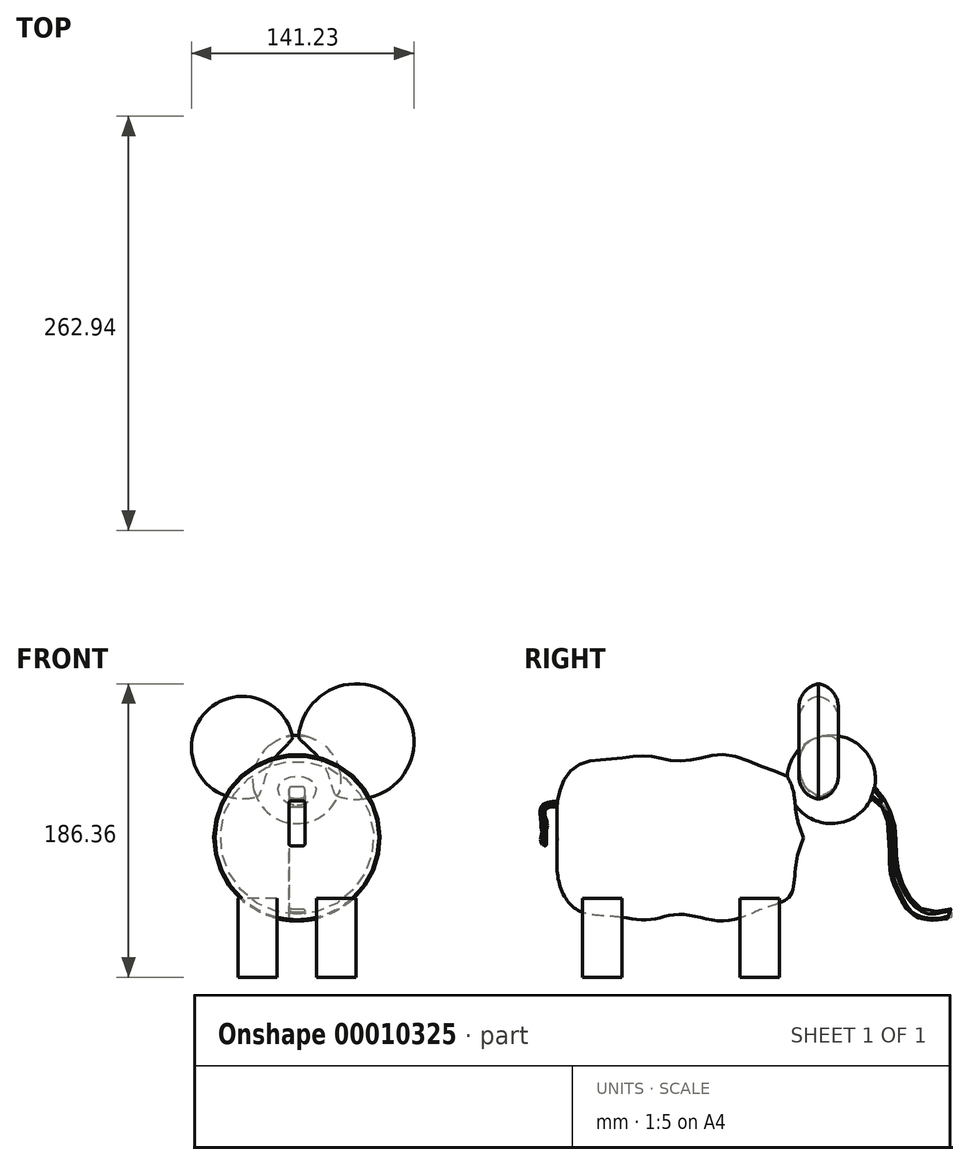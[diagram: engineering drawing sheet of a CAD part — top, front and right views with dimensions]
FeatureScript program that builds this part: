
annotation { "Feature Type Name" : "Feature", "Feature Type Description" : "" }
export const myFeature = defineFeature(function(context is Context, id is Id, definition is map)
    precondition{}
    {
        {
            var Q0;
            Q0=qCreatedBy(makeId("Top.planeOp"),FACE);
            var sketch = newSketch(context, id + "F0", { "sketchPlane" : qUnion([Q0])});
            skLineSegment(sketch, "E0.rect.bottom", {"start": v(25, 50) * mm, "end": v(-25, 50) * mm});
            skLineSegment(sketch, "E0.rect.top", {"start": v(25, -50) * mm, "end": v(-25, -50) * mm});
            skLineSegment(sketch, "E0.rect.left", {"start": v(25, 50) * mm, "end": v(25, -50) * mm});
            skLineSegment(sketch, "E0.rect.right", {"start": v(-25, 50) * mm, "end": v(-25, -50) * mm});
            skPoint(sketch, "E0.rect.middle", {"position": v(0, 0) * mm});
            skCircle(sketch, "E1", {"center": v(-25, 50) * mm, "radius": 12.5 * mm});
            skCircle(sketch, "E2", {"center": v(-25, -50) * mm, "radius": 12.5 * mm});
            skCircle(sketch, "E3", {"center": v(25, -50) * mm, "radius": 12.5 * mm});
            skCircle(sketch, "E4", {"center": v(25, 50) * mm, "radius": 12.5 * mm});
            skSolve(sketch);
        }
        {
            var Q0;
            {var subQ1=sQuery(id+"F0.wireOp",EDGE,"E0.rect.right");var subQ3=sQuery(id+"F0.wireOp",EDGE,"E0.rect.bottom");var subQ5=makeQuery(id+"F0.imprint","INTERSECT",VERTEX,{"derivedFrom":[subQ3,subQ1]});Q0=makeQuery(id+"F0.imprint","IMPRINT",FACE,{"disambiguationData":[TD([[makeQuery(id+"F0.imprint","IMPRINT",EDGE,{"disambiguationData":[TD([[subQ5,1.0]])],"derivedFrom":subQ3}),-1.0]])]});}
            var Q1;
            {var subQ1=sQuery(id+"F0.wireOp",EDGE,"E0.rect.right");var subQ3=sQuery(id+"F0.wireOp",EDGE,"E0.rect.top");var subQ5=makeQuery(id+"F0.imprint","INTERSECT",VERTEX,{"derivedFrom":[subQ3,subQ1]});Q1=makeQuery(id+"F0.imprint","IMPRINT",FACE,{"disambiguationData":[TD([[makeQuery(id+"F0.imprint","IMPRINT",EDGE,{"disambiguationData":[TD([[subQ5,1.0]])],"derivedFrom":subQ3}),1.0]])]});}
            var Q2;
            {var subQ1=sQuery(id+"F0.wireOp",EDGE,"E0.rect.left");var subQ3=sQuery(id+"F0.wireOp",EDGE,"E0.rect.top");var subQ5=makeQuery(id+"F0.imprint","INTERSECT",VERTEX,{"derivedFrom":[subQ3,subQ1]});Q2=makeQuery(id+"F0.imprint","IMPRINT",FACE,{"disambiguationData":[TD([[makeQuery(id+"F0.imprint","IMPRINT",EDGE,{"disambiguationData":[TD([[subQ5,-1.0]])],"derivedFrom":subQ3}),1.0]])]});}
            var Q3;
            {var subQ1=sQuery(id+"F0.wireOp",EDGE,"E0.rect.left");var subQ3=sQuery(id+"F0.wireOp",EDGE,"E0.rect.bottom");var subQ5=makeQuery(id+"F0.imprint","INTERSECT",VERTEX,{"derivedFrom":[subQ3,subQ1]});Q3=makeQuery(id+"F0.imprint","IMPRINT",FACE,{"disambiguationData":[TD([[makeQuery(id+"F0.imprint","IMPRINT",EDGE,{"disambiguationData":[TD([[subQ5,-1.0]])],"derivedFrom":subQ3}),-1.0]])]});}
            var Q4;
            {var subQ1=sQuery(id+"F0.wireOp",EDGE,"E0.rect.right");var subQ3=sQuery(id+"F0.wireOp",EDGE,"E0.rect.bottom");var subQ5=makeQuery(id+"F0.imprint","INTERSECT",VERTEX,{"derivedFrom":[subQ3,subQ1]});Q4=makeQuery(id+"F0.imprint","IMPRINT",FACE,{"disambiguationData":[TD([[makeQuery(id+"F0.imprint","IMPRINT",EDGE,{"disambiguationData":[TD([[subQ5,1.0]])],"derivedFrom":subQ3}),1.0]])]});}
            var Q5;
            {var subQ1=sQuery(id+"F0.wireOp",EDGE,"E0.rect.left");var subQ3=sQuery(id+"F0.wireOp",EDGE,"E0.rect.bottom");var subQ5=makeQuery(id+"F0.imprint","INTERSECT",VERTEX,{"derivedFrom":[subQ3,subQ1]});Q5=makeQuery(id+"F0.imprint","IMPRINT",FACE,{"disambiguationData":[TD([[makeQuery(id+"F0.imprint","IMPRINT",EDGE,{"disambiguationData":[TD([[subQ5,-1.0]])],"derivedFrom":subQ3}),1.0]])]});}
            var Q6;
            {var subQ1=sQuery(id+"F0.wireOp",EDGE,"E0.rect.left");var subQ3=sQuery(id+"F0.wireOp",EDGE,"E0.rect.top");var subQ5=makeQuery(id+"F0.imprint","INTERSECT",VERTEX,{"derivedFrom":[subQ3,subQ1]});Q6=makeQuery(id+"F0.imprint","IMPRINT",FACE,{"disambiguationData":[TD([[makeQuery(id+"F0.imprint","IMPRINT",EDGE,{"disambiguationData":[TD([[subQ5,-1.0]])],"derivedFrom":subQ3}),-1.0]])]});}
            var Q7;
            {var subQ1=sQuery(id+"F0.wireOp",EDGE,"E0.rect.right");var subQ3=sQuery(id+"F0.wireOp",EDGE,"E0.rect.top");var subQ5=makeQuery(id+"F0.imprint","INTERSECT",VERTEX,{"derivedFrom":[subQ3,subQ1]});Q7=makeQuery(id+"F0.imprint","IMPRINT",FACE,{"disambiguationData":[TD([[makeQuery(id+"F0.imprint","IMPRINT",EDGE,{"disambiguationData":[TD([[subQ5,1.0]])],"derivedFrom":subQ3}),-1.0]])]});}
            extrude(context, id + "F1", {"entities" : qUnion([Q0, Q1, Q2, Q3, Q4, Q5, Q6, Q7]), "depth" : 50 * mm});
        }
        {
            var Q0;
            Q0=qCreatedBy(makeId("Right.planeOp"),FACE);
            var sketch = newSketch(context, id + "F2", { "sketchPlane" : qUnion([Q0])});
            skLineSegment(sketch, "E5", {"start": v(77.76, 40) * mm, "end": v(77.76, 88.55) * mm, "construction": true});
            skLineSegment(sketch, "E6", {"start": v(77.76, 88.55) * mm, "end": v(-77.67, 88.55) * mm, "construction": true});
            skLineSegment(sketch, "E7", {"start": v(-77.67, 88.55) * mm, "end": v(-77.67, 40) * mm, "construction": true});
            skLineSegment(sketch, "E8.0", {"start": v(37.5, 50) * mm, "end": v(62.5, 50) * mm});
            skFitSpline(sketch, "E9", {"points": [v(77.76, 88.55) * mm, v(73.01, 71.56) * mm, v(69.46, 51.72) * mm, v(54.36, 44.32) * mm, v(28.3, 35.74) * mm, v(0, 39.88) * mm, v(-19.95, 36.63) * mm, v(-41.56, 38.4) * mm, v(-65.54, 42.55) * mm, v(-77.67, 61.5) * mm, v(-77.67, 88.55) * mm], "startDerivative": vector(-63.66, -186.12) * mm, "endDerivative": vector(26.08, 252.74) * mm});
            skLineSegment(sketch, "E10", {"start": v(77.76, 88.55) * mm, "end": v(-77.67, 88.55) * mm});
            skSolve(sketch);
        }
        {
            var Q0;
            Q0=makeQuery(id+"F2.imprint","IMPRINT",FACE,{"disambiguationData":[TD([[makeQuery(id+"F2.imprint","IMPRINT",EDGE,{"derivedFrom":sQuery(id+"F2.wireOp",EDGE,"E9")}),-1.0]])]});
            var Q1;
            Q1=sQuery(id+"F2.wireOp",EDGE,"E10");
            revolve(context, id + "F3", {"entities" : qUnion([Q0]), "axis" : qUnion([Q1]), "revolveType" : RevolveType.FULL});
        }
        {
            var Q0;
            Q0=qCreatedBy(makeId("Right.planeOp"),FACE);
            var sketch = newSketch(context, id + "F4", { "sketchPlane" : qUnion([Q0])});
            skArc(sketch, "E11", {"start": v(95.55, 97.55) * mm, "mid": v(123.61, 125.6) * mm, "end": v(95.55, 153.66) * mm});
            skLineSegment(sketch, "E12", {"start": v(95.55, 125.6) * mm, "end": v(95.55, 153.66) * mm});
            skLineSegment(sketch, "E13", {"start": v(95.55, 153.66) * mm, "end": v(95.55, 125.6) * mm});
            skLineSegment(sketch, "E14", {"start": v(95.55, 125.6) * mm, "end": v(95.55, 97.55) * mm});
            skSolve(sketch);
        }
        {
            var Q0;
            Q0=makeQuery(id+"F4.imprint","IMPRINT",FACE,{"disambiguationData":[TD([[makeQuery(id+"F4.imprint","IMPRINT",EDGE,{"derivedFrom":sQuery(id+"F4.wireOp",EDGE,"E11")}),1.0]])]});
            var Q1;
            Q1=sQuery(id+"F4.wireOp",EDGE,"E13");
            revolve(context, id + "F5", {"operationType" : NewBodyOperationType.ADD, "entities" : qUnion([Q0]), "axis" : qUnion([Q1]), "revolveType" : RevolveType.FULL});
        }
        {
            var Q0;
            Q0=qCreatedBy(makeId("Right.planeOp"),FACE);
            var sketch = newSketch(context, id + "F6", { "sketchPlane" : qUnion([Q0])});
            skFitSpline(sketch, "E15", {"points": [v(119.26, 122.77) * mm, v(134.74, 100.97) * mm, v(137.86, 69.03) * mm, v(156.47, 41.97) * mm, v(171.9, 43.27) * mm, v(173.28, 39.82) * mm, v(168.3, 36.67) * mm, v(148.86, 38.32) * mm, v(139, 50.83) * mm, v(133.64, 63.44) * mm, v(132.41, 77.6) * mm, v(131.43, 97.92) * mm, v(127.97, 107.74) * mm, v(117.03, 118.44) * mm, v(119.26, 122.77) * mm]});
            skSolve(sketch);
        }
        {
            var Q0;
            Q0=makeQuery(id+"F6.imprint","IMPRINT",FACE,{"disambiguationData":[TD([[makeQuery(id+"F6.imprint","IMPRINT",EDGE,{"derivedFrom":sQuery(id+"F6.wireOp",EDGE,"E15")}),-1.0]])]});
            extrude(context, id + "F7", {"entities" : qUnion([Q0]), "operationType" : NewBodyOperationType.ADD, "depth" : 5 * mm, "hasSecondDirection" : true, "secondDirectionOppositeDirection" : true, "secondDirectionDepth" : 5 * mm});
        }
        {
            var Q0;
            Q0=makeQuery(id+"F7.opExtrude","CAP_EDGE",EDGE,{"disambiguationData":[OSD([sQuery(id+"F6.wireOp",EDGE,"E15")])],"isStart":false});
            var Q1;
            Q1=makeQuery(id+"F7.opExtrude","CAP_EDGE",EDGE,{"disambiguationData":[OSD([sQuery(id+"F6.wireOp",EDGE,"E15")])],"isStart":true});
            fillet(context, id + "F8", {"entities" : qUnion([Q0, Q1]), "radius" : 1.56 * mm, "tangentPropagation" : true, "allowEdgeOverflow" : false});
        }
        {
            var Q0;
            Q0=qCreatedBy(makeId("Right.planeOp"),FACE);
            var sketch = newSketch(context, id + "F9", { "sketchPlane" : qUnion([Q0])});
            skFitSpline(sketch, "E16", {"points": [v(-74.2, 108.68) * mm, v(-82.32, 108.2) * mm, v(-86.3, 105.3) * mm, v(-84.81, 97.1) * mm, v(-85.45, 91.73) * mm, v(-85.75, 83.62) * mm, v(-88.83, 85.87) * mm, v(-88.25, 91.73) * mm, v(-88.8, 96.23) * mm, v(-89.02, 100.25) * mm, v(-89.5, 104.25) * mm, v(-88.91, 107.84) * mm, v(-85.93, 110.64) * mm, v(-80.18, 111.67) * mm, v(-73.52, 111.52) * mm, v(-74.2, 108.68) * mm]});
            skSolve(sketch);
        }
        {
            var Q0;
            Q0=makeQuery(id+"F9.imprint","IMPRINT",FACE,{"disambiguationData":[TD([[makeQuery(id+"F9.imprint","IMPRINT",EDGE,{"derivedFrom":sQuery(id+"F9.wireOp",EDGE,"E16")}),-1.0]])]});
            extrude(context, id + "F10", {"entities" : qUnion([Q0]), "operationType" : NewBodyOperationType.ADD, "depth" : 5 * mm, "hasSecondDirection" : true, "secondDirectionOppositeDirection" : true, "secondDirectionDepth" : 5 * mm});
        }
        {
            var Q0;
            Q0=makeQuery(id+"F10.opExtrude","CAP_EDGE",EDGE,{"disambiguationData":[OSD([sQuery(id+"F9.wireOp",EDGE,"E16")])],"isStart":true});
            var Q1;
            Q1=makeQuery(id+"F10.opExtrude","CAP_EDGE",EDGE,{"disambiguationData":[OSD([sQuery(id+"F9.wireOp",EDGE,"E16")])],"isStart":false});
            fillet(context, id + "F11", {"entities" : qUnion([Q0, Q1]), "radius" : 1 * mm, "tangentPropagation" : true, "allowEdgeOverflow" : false});
        }
        {
            var Q0;
            Q0=qCreatedBy(makeId("Front.planeOp"),FACE);
            cPlane(context, id + "F12", {"entities" : qUnion([Q0]), "cplaneType" : CPlaneType.OFFSET, "offset" : 100 * mm, "oppositeDirection" : true, "width" : 150 * mm, "height" : 150 * mm});
        }
        {
            var Q0;
            Q0=qCreatedBy(id+"F12.planeOp",FACE);
            var sketch = newSketch(context, id + "F13", { "sketchPlane" : qUnion([Q0])});
            skCircle(sketch, "E17", {"center": v(-34.47, 145.87) * mm, "radius": 32.7 * mm});
            skCircle(sketch, "E18", {"center": v(37.6, 149.68) * mm, "radius": 36.89 * mm});
            skSolve(sketch);
        }
        {
            var Q0;
            Q0=makeQuery(id+"F13.imprint","IMPRINT",FACE,{"disambiguationData":[TD([[makeQuery(id+"F13.imprint","IMPRINT",EDGE,{"derivedFrom":sQuery(id+"F13.wireOp",EDGE,"E18")}),1.0]])]});
            var Q1;
            Q1=makeQuery(id+"F13.imprint","IMPRINT",FACE,{"disambiguationData":[TD([[makeQuery(id+"F13.imprint","IMPRINT",EDGE,{"derivedFrom":sQuery(id+"F13.wireOp",EDGE,"E17")}),1.0]])]});
            extrude(context, id + "F14", {"entities" : qUnion([Q0, Q1]), "operationType" : NewBodyOperationType.ADD, "depth" : 25 * mm});
        }
        {
            var Q0;
            Q0=makeQuery(id+"F14.opExtrude","CAP_EDGE",EDGE,{"disambiguationData":[OSD([sQuery(id+"F13.wireOp",EDGE,"E17")])],"isStart":true});
            var Q1;
            Q1=makeQuery(id+"F14.opExtrude","CAP_EDGE",EDGE,{"disambiguationData":[OSD([sQuery(id+"F13.wireOp",EDGE,"E18")])],"isStart":true});
            var Q2;
            Q2=makeQuery(id+"F14.opExtrude","CAP_EDGE",EDGE,{"disambiguationData":[OSD([sQuery(id+"F13.wireOp",EDGE,"E18")])],"isStart":false});
            var Q3;
            Q3=makeQuery(id+"F14.opExtrude","CAP_EDGE",EDGE,{"disambiguationData":[OSD([sQuery(id+"F13.wireOp",EDGE,"E17")])],"isStart":false});
            fillet(context, id + "F15", {"entities" : qUnion([Q0, Q1, Q2, Q3]), "radius" : 15 * mm, "tangentPropagation" : true, "allowEdgeOverflow" : false});
        }
    });
